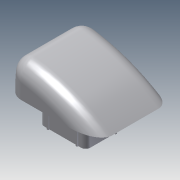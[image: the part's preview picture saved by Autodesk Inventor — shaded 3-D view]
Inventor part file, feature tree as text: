
AUTODESK INVENTOR PART (.ipt)
format: ipt  version: 2015 (Build 190159000, 159)  size: 419,328 bytes
history: native  units: in
note: dims shown in document units (in); Inventor stores cm internally (conversion verified against a paired STEP export)
features: extrude x5, sketch x5, projected_geometry x4, plane x3, mirror x2, fillet x1, shell x1, pattern_linear x1
ambient origin geometry x8: Origin, YZ Plane, XZ Plane, XY Plane, X Axis, Y Axis, Z Axis, Center Point
bodies: Body1 (feature_tree)
feature tree (22):
  extrude  "Extrusion2"  Depth=6.0in
  fillet  "Fillet2"  Radius=0.64in
  shell  "Shell1"  Thickness=6.0in
  plane  "Work Plane1"
  extrude  "Extrusion3"  Depth=6.0in
  extrude  "Extrusion4"  Depth=0.5in
  extrude  "Extrusion5"  TaperAngle=0.0deg  [1 undecoded]
  pattern_linear  "Rectangular Pattern1"  Spacing1=2.22in  [1 undecoded]
  plane  "Work Plane2"
  mirror  "Mirror1"
  extrude  "Extrusion6"  Depth=0.04in
  plane  "Work Plane3"
  mirror  "Mirror2"
  sketch  "Sketch4"  dims[d11=3.04in d14=3.01in d15=0.64in d17=6.0in]
  sketch  "Sketch5"  dims[d18=6.0in d19=0.4in]
  projected_geometry  "Projected Loop1"
  sketch  "Sketch6"  dims[d20=2.55in d21=0.0in d22=0.5in]
  projected_geometry  "Projected Loop2"
  sketch  "Sketch7"  dims[d23=0.07in d24=0.0in]
  projected_geometry  "Projected Loop3"
  sketch  "Sketch8"  dims[d25=0.68in d26=2.22in d27=0.29in d28=2.26in d29=0.15in d30=0.05in d31=2.55in d32=0.0in d33=0.67in d34=0.0in d35=0.05in d36=0.04in d37=0.925in d38=0.67in d39=0.0in d40=0.7874in d42=0.965in d43=0.04in d44=0.025in d45=0.025in d46=0.67in d47=0.0in]
  projected_geometry  "Projected Loop4"
note: 2 required parameter values undecoded (feature->parameter linkage not recoverable at this tier; creation-order binding heuristic only, values carry confidence <= 0.55)
